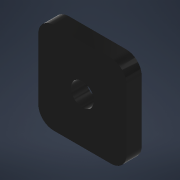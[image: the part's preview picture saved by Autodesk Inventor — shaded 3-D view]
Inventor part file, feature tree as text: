
AUTODESK INVENTOR PART (.ipt)
format: ipt  version: 2021 (Build 250183000, 183)  size: 106,496 bytes
history: native  units: mm
features: other x5, reference x2, extrude x1
ambient origin geometry x8: Origin, YZ Plane, XZ Plane, XY Plane, X Axis, Y Axis, Z Axis, Center Point
bodies: Solid1 (feature_tree)
feature tree (8):
  extrude  "washer"  Depth=12.0mm
  other  "washer_sketch"
  reference  "Reference1"
  reference  "Reference2"
  other  "<userpath>\Documents\Dev\tco-cad\camera_mount\assembly_camera_mount.iam"
  other  "assembly_camera_mount.iam"
  other  "linear_stepper_base:1"
  other  "mount_linear_stepper:1"
